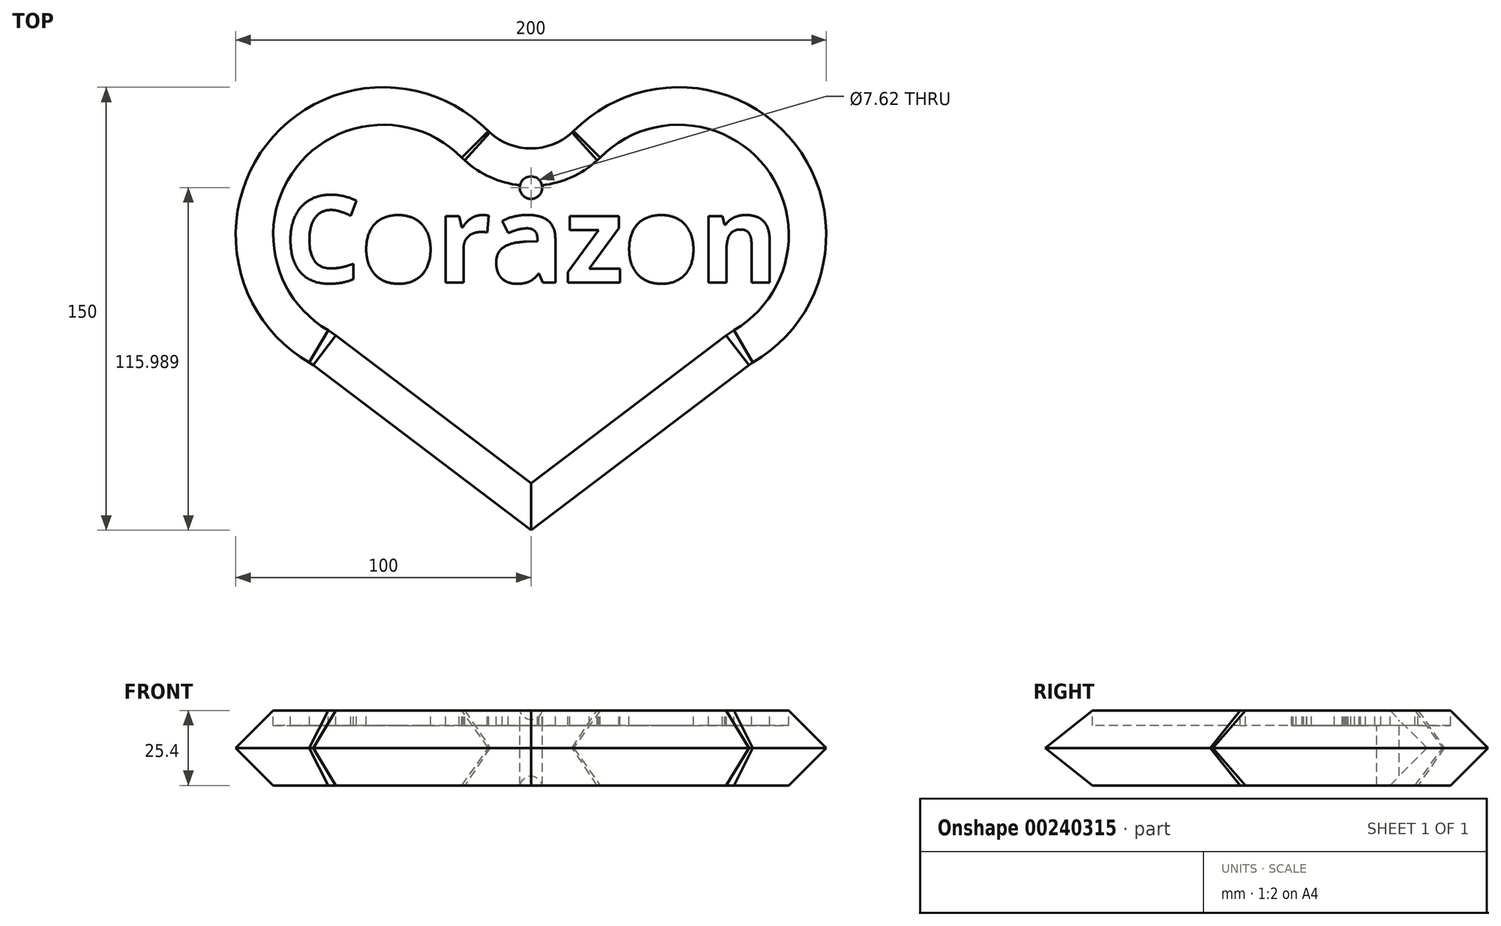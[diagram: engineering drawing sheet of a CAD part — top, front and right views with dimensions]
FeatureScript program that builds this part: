
annotation { "Feature Type Name" : "Feature", "Feature Type Description" : "" }
export const myFeature = defineFeature(function(context is Context, id is Id, definition is map)
    precondition{}
    {
        {
            var Q0;
            Q0=qCreatedBy(makeId("Top.planeOp"),FACE);
            var sketch = newSketch(context, id + "F0", { "sketchPlane" : qUnion([Q0])});
            skLineSegment(sketch, "E0.bottom", {"start": v(50, 50) * mm, "end": v(-50, 50) * mm, "construction": true});
            skLineSegment(sketch, "E0.top", {"start": v(50, -50) * mm, "end": v(-50, -50) * mm, "construction": true});
            skLineSegment(sketch, "E0.left", {"start": v(50, 50) * mm, "end": v(50, -50) * mm, "construction": true});
            skLineSegment(sketch, "E0.right", {"start": v(-50, 50) * mm, "end": v(-50, -50) * mm, "construction": true});
            skPoint(sketch, "E0.middle", {"position": v(0, 0) * mm});
            skArc(sketch, "E1", {"start": v(-14.23, 84.94) * mm, "mid": v(-89.68, 80.42) * mm, "end": v(-74.45, 6.39) * mm});
            skArc(sketch, "E2", {"start": v(74.45, 6.39) * mm, "mid": v(89.68, 80.42) * mm, "end": v(14.23, 84.94) * mm});
            skLineSegment(sketch, "E3", {"start": v(-50, 50) * mm, "end": v(-100, 50) * mm, "construction": true});
            skLineSegment(sketch, "E4", {"start": v(50, 50) * mm, "end": v(100, 50) * mm, "construction": true});
            skLineSegment(sketch, "E5", {"start": v(-50, 50) * mm, "end": v(-85.36, 14.64) * mm, "construction": true});
            skLineSegment(sketch, "E6", {"start": v(50, 50) * mm, "end": v(85.36, 14.64) * mm, "construction": true});
            skLineSegment(sketch, "E7", {"start": v(-85.36, 14.64) * mm, "end": v(0, -50) * mm});
            skLineSegment(sketch, "E8", {"start": v(0, -50) * mm, "end": v(85.36, 14.64) * mm});
            skLineSegment(sketch, "E9", {"start": v(-50, 50) * mm, "end": v(-50, 100) * mm, "construction": true});
            skLineSegment(sketch, "E10", {"start": v(50, 50) * mm, "end": v(50, 100) * mm, "construction": true});
            skLineSegment(sketch, "E11", {"start": v(-50, 100) * mm, "end": v(50, 100) * mm, "construction": true});
            skArc(sketch, "E12", {"start": v(15.06, 85.77) * mm, "mid": v(0.58, 79.29) * mm, "end": v(-14.23, 84.94) * mm, "construction": true});
            skArc(sketch, "E13", {"start": v(-14.23, 84.94) * mm, "mid": v(0, 79.28) * mm, "end": v(14.23, 84.94) * mm});
            skSolve(sketch);
        }
        {
            var Q0;
            Q0 = qSketchRegion(id + "F0", true);
            extrude(context, id + "F1", {"entities" : qUnion([Q0]), "depth" : 25.4 * mm});
        }
        {
            var Q0;
            Q0=makeQuery(id+"F1.opExtrude","CAP_FACE",FACE,{"disambiguationData":[OSD([sQuery(id+"F0.wireOp",EDGE,"E1"),sQuery(id+"F0.wireOp",EDGE,"E2"),sQuery(id+"F0.wireOp",EDGE,"E7"),sQuery(id+"F0.wireOp",EDGE,"E8"),sQuery(id+"F0.wireOp",EDGE,"E13")])],"isStart":false});
            var Q1;
            Q1=makeQuery(id+"F1.opExtrude","SWEPT_FACE",FACE,{"disambiguationData":[OSD([sQuery(id+"F0.wireOp",EDGE,"E2")])]});
            var Q2;
            Q2=makeQuery(id+"F1.opExtrude","SWEPT_FACE",FACE,{"disambiguationData":[OSD([sQuery(id+"F0.wireOp",EDGE,"E1")])]});
            chamfer(context, id + "F2", {"entities" : qUnion([Q0, Q1, Q2]), "width" : 12.7 * mm, "tangentPropagation" : true});
        }
        {
            var Q0;
            Q0=makeQuery(id+"F1.opExtrude","CAP_FACE",FACE,{"disambiguationData":[OSD([sQuery(id+"F0.wireOp",EDGE,"E1"),sQuery(id+"F0.wireOp",EDGE,"E2"),sQuery(id+"F0.wireOp",EDGE,"E7"),sQuery(id+"F0.wireOp",EDGE,"E8"),sQuery(id+"F0.wireOp",EDGE,"E13")])],"isStart":false});
            var sketch = newSketch(context, id + "F3", { "sketchPlane" : qUnion([Q0])});
            skText(sketch, "E14", { "text": "Corazon\n", "fontName": "OpenSans-Bold.ttf"});
            const initialGuessF3  = {"E14": [-0.08385, 0.03385, 1, 0, 0.02961]};
            skSetInitialGuess(sketch, initialGuessF3);
            skSolve(sketch);
        }
        {
            var Q0;
            Q0=makeQuery(id+"F3.imprint","IMPRINT",FACE,{"disambiguationData":[TD([[makeQuery(id+"F3.imprint","IMPRINT",EDGE,{"derivedFrom":sQuery(id+"F3.wireOp",EDGE,"E14.sketch_text.stroke-0")}),1.0]])]});
            var sketch = newSketch(context, id + "F4", { "sketchPlane" : qUnion([Q0])});
            skCircle(sketch, "E15", {"center": v(0, 65.99) * mm, "radius": 3.81 * mm});
            skLineSegment(sketch, "E16", {"start": v(0, 10.1) * mm, "end": v(0, 65.99) * mm, "construction": true});
            skSolve(sketch);
        }
        {
            var Q0;
            Q0 = qSketchRegion(id + "F4", true);
            extrude(context, id + "F5", {"entities" : qUnion([Q0]), "operationType" : NewBodyOperationType.REMOVE, "oppositeDirection" : true, "depth" : 25.4 * mm});
        }
        {
            var Q0;
            Q0=makeQuery(id+"F3.imprint","IMPRINT",FACE,{"disambiguationData":[TD([[makeQuery(id+"F3.imprint","IMPRINT",EDGE,{"derivedFrom":sQuery(id+"F3.wireOp",EDGE,"E14.sketch_text.stroke-0")}),1.0]])]});
            extrude(context, id + "F6", {"entities" : qUnion([Q0]), "operationType" : NewBodyOperationType.REMOVE, "oppositeDirection" : true, "depth" : 5.08 * mm});
        }
    });
